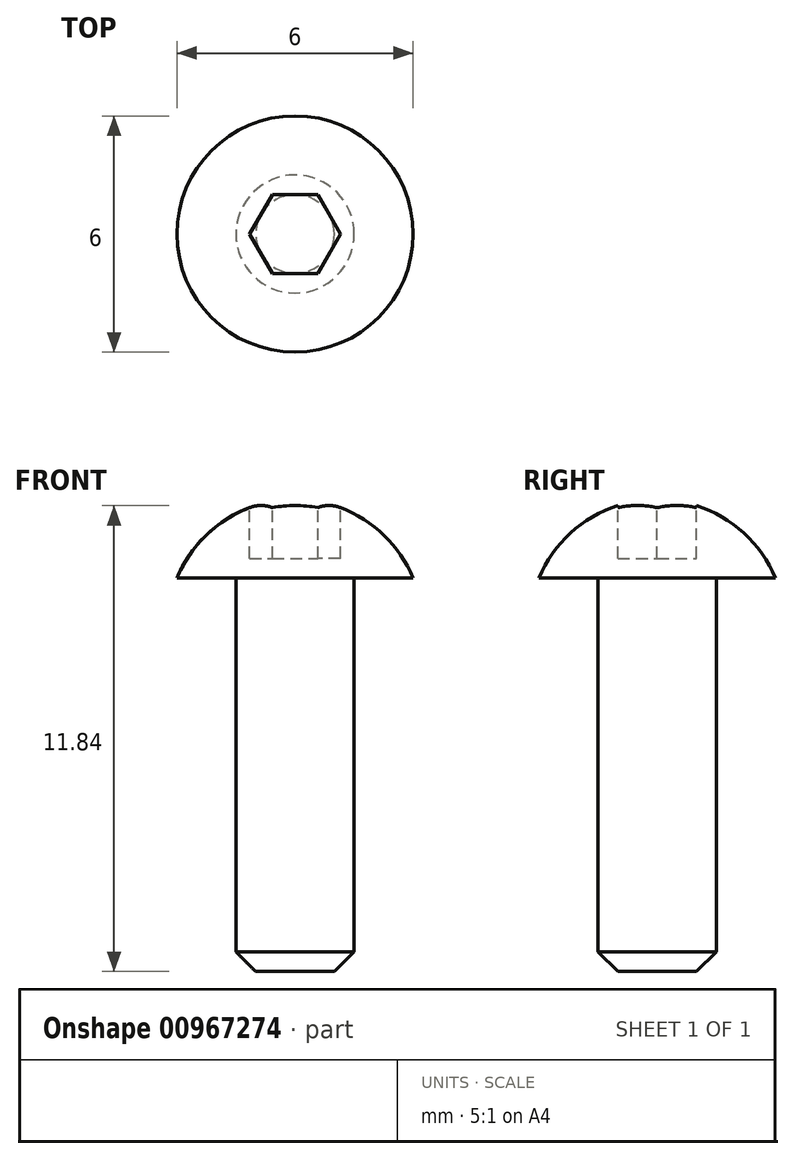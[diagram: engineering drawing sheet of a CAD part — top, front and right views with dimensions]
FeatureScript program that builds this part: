
annotation { "Feature Type Name" : "Feature", "Feature Type Description" : "" }
export const myFeature = defineFeature(function(context is Context, id is Id, definition is map)
    precondition{}
    {
        {
            var Q0;
            Q0=qCreatedBy(makeId("Front.planeOp"),FACE);
            var sketch = newSketch(context, id + "F0", { "sketchPlane" : qUnion([Q0])});
            skLineSegment(sketch, "E0", {"start": v(0, 0) * mm, "end": v(0, 12) * mm});
            skLineSegment(sketch, "E1", {"start": v(0, 0) * mm, "end": v(1.5, 0) * mm});
            skLineSegment(sketch, "E2", {"start": v(1.5, 0) * mm, "end": v(1.5, 10) * mm});
            skLineSegment(sketch, "E3", {"start": v(1.5, 10) * mm, "end": v(3, 10) * mm});
            skArc(sketch, "E4", {"start": v(3, 10) * mm, "mid": v(1.8, 11.45) * mm, "end": v(0, 12) * mm});
            skSolve(sketch);
        }
        {
            var Q0;
            Q0=qSketchRegion(id+"F0",true);
            var Q1;
            Q1=sQuery(id+"F0.wireOp",EDGE,"E0");
            revolve(context, id + "F1", {"entities" : qUnion([Q0]), "axis" : qUnion([Q1]), "revolveType" : RevolveType.FULL});
        }
        {
            var Q0;
            Q0=makeQuery(id+"F1.opRevolve","SWEPT_EDGE",EDGE,{"disambiguationData":[OSD([sQuery(id+"F0.wireOp",EDGE,"E1"),sQuery(id+"F0.wireOp",EDGE,"E2")])]});
            chamfer(context, id + "F2", {"entities" : qUnion([Q0]), "width" : 0.5 * mm, "tangentPropagation" : true});
        }
        {
            var Q0;
            Q0=qCreatedBy(makeId("Top.planeOp"),FACE);
            cPlane(context, id + "F3", {"entities" : qUnion([Q0]), "cplaneType" : CPlaneType.OFFSET, "offset" : 12 * mm, "width" : 150 * mm, "height" : 150 * mm});
        }
        {
            var Q0;
            Q0=qCreatedBy(id+"F3.planeOp",FACE);
            var sketch = newSketch(context, id + "F4", { "sketchPlane" : qUnion([Q0])});
            skCircle(sketch, "E5.cCircle", {"center": v(0, 0) * mm, "radius": 1 * mm, "construction": true});
            skLineSegment(sketch, "E5.0", {"start": v(-0.58, 1) * mm, "end": v(0.58, 1) * mm});
            skLineSegment(sketch, "E5.1", {"start": v(0.58, 1) * mm, "end": v(1.15, 0) * mm});
            skLineSegment(sketch, "E5.2", {"start": v(1.15, 0) * mm, "end": v(0.58, -1) * mm});
            skLineSegment(sketch, "E5.3", {"start": v(0.58, -1) * mm, "end": v(-0.58, -1) * mm});
            skLineSegment(sketch, "E5.4", {"start": v(-0.58, -1) * mm, "end": v(-1.15, 0) * mm});
            skLineSegment(sketch, "E5.5", {"start": v(-1.15, 0) * mm, "end": v(-0.58, 1) * mm});
            skPoint(sketch, "E5.0.midPoint", {"position": v(0, 1) * mm});
            skSolve(sketch);
        }
        {
            var Q0;
            Q0=qSketchRegion(id+"F4",true);
            extrude(context, id + "F5", {"entities" : qUnion([Q0]), "operationType" : NewBodyOperationType.REMOVE, "oppositeDirection" : true, "depth" : 1.5 * mm});
        }
    });
